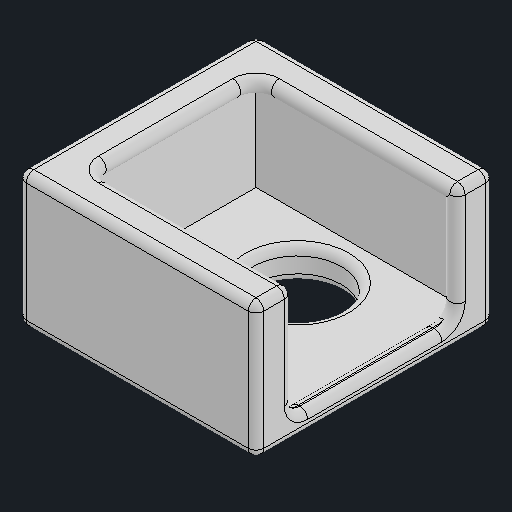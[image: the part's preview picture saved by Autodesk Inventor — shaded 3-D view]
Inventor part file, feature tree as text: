
AUTODESK INVENTOR PART (.ipt)
format: ipt  version: 2024.2 (Build 282272000, 272)  size: 182,272 bytes
history: native  units: mm
features: other x1, fillet x1
ambient origin geometry x8: Origin, YZ Plane, XZ Plane, XY Plane, X Axis, Y Axis, Z Axis, Center Point
bodies: Body1 (feature_tree)
feature tree (2):
  other  "솔리드1"
  fillet  "Fillet2"  [1 undecoded]
note: 1 required parameter value undecoded (feature->parameter linkage not recoverable at this tier; creation-order binding heuristic only, values carry confidence <= 0.55)
